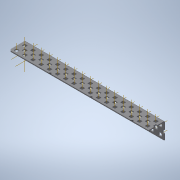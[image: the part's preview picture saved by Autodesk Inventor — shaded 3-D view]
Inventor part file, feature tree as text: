
AUTODESK INVENTOR PART (.ipt)
format: ipt  version: 2020 (Build 240168000, 168)  size: 2,149,376 bytes
history: native  units: in
note: dims shown in document units (in); Inventor stores cm internally (conversion verified against a paired STEP export)
features: other x107, pattern_linear x4, sheet_metal_op x1, extrude x1, plane x1, split x1, imported_body x1, sketch x1
ambient origin geometry x8: Origin, YZ Plane, XZ Plane, XY Plane, X Axis, Y Axis, Z Axis, Center Point
bodies: Body1 (feature_tree)
feature tree (117):
  sheet_metal_op  "Fold1"
  other  "L-Channel"
  extrude  "length cut"  Depth=0.5in
  other  "top out axis"
  other  "top inner axis"
  other  "back out axis"
  other  "back inner axis"
  pattern_linear  "top outer axes"  Count1=2 Spacing1=0.5in
  pattern_linear  "top inner axes"  Spacing1=0.5in  [1 undecoded]
  pattern_linear  "back outer axes"  Count1=2 Spacing1=0.5in
  pattern_linear  "back inner axes"  Spacing1=0.5in  [1 undecoded]
  other  "right plane"
  plane  "Work Plane3"
  split  "Split1"
  imported_body  "Base1"
  sketch  "Sketch1"  dims[d1=0.0in d4=0.5in d5=0.7874in d7=0.5in d10=0.5in d13=0.5in d14=0.7874in d16=0.5in d19=0.5in d20=-9.0in d21=0.0in d22=0.0in d23=0.0in d24=0.0in d25=0.0in d26=0.0in]
  other  "Work Point1"
  other  "Work Point2"
  other  "Work Point3"
  other  "Work Point4"
  other  "Work Axis5"
  other  "Work Axis6"
  other  "Work Axis7"
  other  "Work Axis8"
  other  "Work Axis11"
  other  "Work Axis12"
  other  "Work Axis13"
  other  "Work Axis14"
  other  "Work Axis15"
  other  "Work Axis18"
  other  "Work Axis19"
  other  "Work Axis20"
  other  "Work Axis23"
  other  "Work Axis24"
  other  "Work Axis25"
  other  "Work Axis26"
  other  "Work Axis29"
  other  "Work Axis30"
  other  "Work Axis31"
  other  "Work Axis32"
  other  "Work Axis33"
  other  "Work Axis36"
  other  "Work Axis37"
  other  "Work Axis38"
  other  "Work Axis41"
  other  "Work Axis42"
  other  "Work Axis43"
  other  "Work Axis44"
  other  "Work Axis45"
  other  "Work Axis46"
  other  "Work Axis47"
  other  "Work Axis48"
  other  "Work Axis49"
  other  "Work Axis50"
  other  "Work Axis51"
  other  "Work Axis52"
  other  "Work Axis61"
  other  "Work Axis62"
  other  "Work Axis63"
  other  "Work Axis64"
  other  "Work Axis65"
  other  "Work Axis66"
  other  "Work Axis67"
  other  "Work Axis68"
  other  "Work Axis69"
  other  "Work Axis70"
  other  "Work Axis71"
  other  "Work Axis72"
  other  "Work Axis81"
  other  "Work Axis82"
  other  "Work Axis83"
  other  "Work Axis84"
  other  "Work Axis85"
  other  "Work Axis86"
  other  "Work Axis87"
  other  "Work Axis88"
  other  "Work Axis89"
  other  "Work Axis90"
  other  "Work Axis91"
  other  "Work Axis92"
  other  "Work Axis101"
  other  "Work Axis102"
  other  "Work Axis103"
  other  "Work Axis104"
  other  "Work Axis105"
  other  "Work Axis106"
  other  "Work Axis107"
  other  "Work Axis108"
  other  "Work Axis109"
  other  "Work Axis110"
  other  "Work Axis111"
  other  "Work Axis112"
  other  "Work Axis121"
  other  "Work Axis122"
  other  "Work Axis123"
  other  "Work Axis124"
  other  "Work Axis125"
  other  "Work Axis126"
  other  "Work Axis127"
  other  "Work Axis128"
  other  "Work Axis129"
  other  "Work Axis130"
  other  "Work Axis131"
  other  "Work Axis132"
  other  "Work Axis141"
  other  "Work Axis142"
  other  "Work Axis143"
  other  "Work Axis144"
  other  "Work Axis145"
  other  "Work Axis146"
  other  "Work Axis147"
  other  "Work Axis148"
  other  "Work Axis149"
  other  "Work Axis150"
  other  "Work Axis151"
  other  "Work Axis152"
  other  "left plane"
note: 2 required parameter values undecoded (feature->parameter linkage not recoverable at this tier; creation-order binding heuristic only, values carry confidence <= 0.55)
